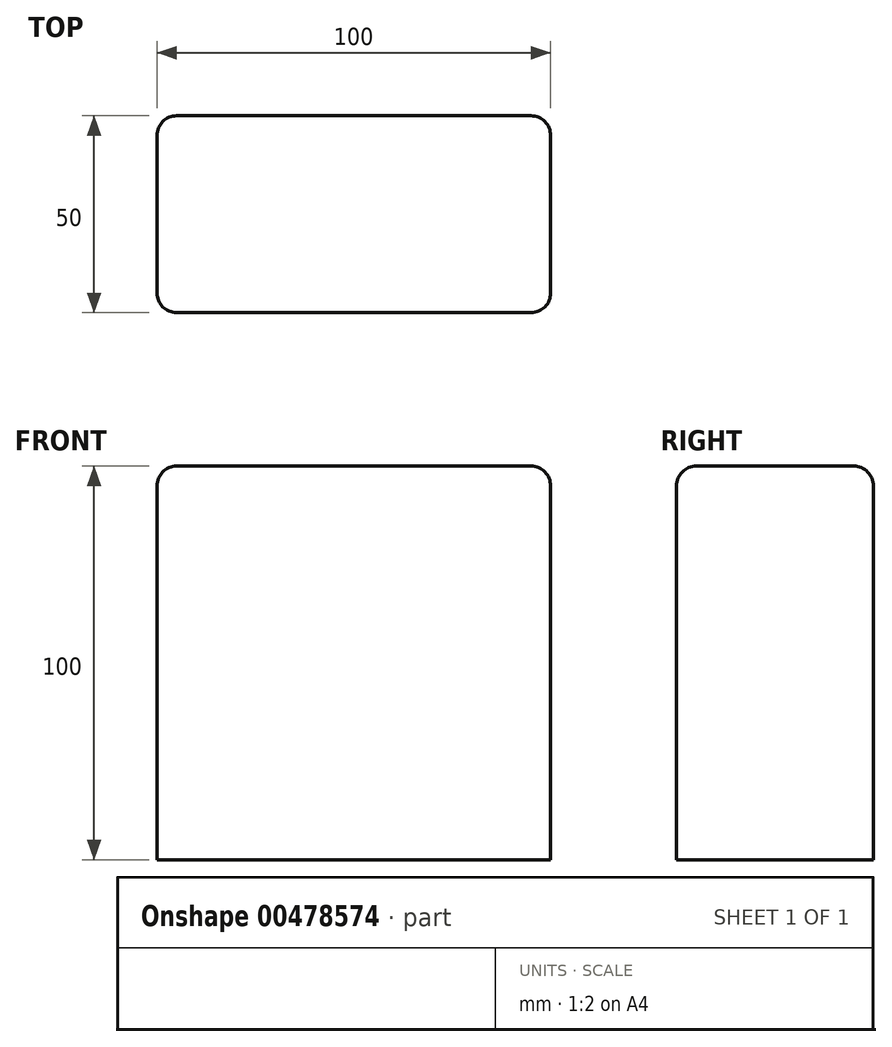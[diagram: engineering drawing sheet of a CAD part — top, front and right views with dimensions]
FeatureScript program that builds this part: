
annotation { "Feature Type Name" : "Feature", "Feature Type Description" : "" }
export const myFeature = defineFeature(function(context is Context, id is Id, definition is map)
    precondition{}
    {
        {
            var Q0;
            Q0=qCreatedBy(makeId("Top.planeOp"),FACE);
            var sketch = newSketch(context, id + "F0", { "sketchPlane" : qUnion([Q0])});
            skLineSegment(sketch, "E0.bottom", {"start": v(-40.12, 7.75) * mm, "end": v(59.88, 7.75) * mm});
            skLineSegment(sketch, "E0.top", {"start": v(-40.12, -42.25) * mm, "end": v(59.88, -42.25) * mm});
            skLineSegment(sketch, "E0.left", {"start": v(-40.12, 7.75) * mm, "end": v(-40.12, -42.25) * mm});
            skLineSegment(sketch, "E0.right", {"start": v(59.88, 7.75) * mm, "end": v(59.88, -42.25) * mm});
            skSolve(sketch);
        }
        {
            var Q0;
            Q0=makeQuery(id+"F0.imprint","IMPRINT",FACE,{"disambiguationData":[TD([[makeQuery(id+"F0.imprint","IMPRINT",EDGE,{"derivedFrom":sQuery(id+"F0.wireOp",EDGE,"E0.bottom")}),-1.0]])]});
            extrude(context, id + "F1", {"entities" : qUnion([Q0]), "depth" : 100 * mm});
        }
        {
            var Q0;
            Q0=makeQuery(id+"F1.opExtrude","CAP_EDGE",EDGE,{"disambiguationData":[OSD([sQuery(id+"F0.wireOp",EDGE,"E0.top")])],"isStart":false});
            var Q1;
            Q1=makeQuery(id+"F1.opExtrude","CAP_EDGE",EDGE,{"disambiguationData":[OSD([sQuery(id+"F0.wireOp",EDGE,"E0.bottom")])],"isStart":false});
            var Q2;
            Q2=makeQuery(id+"F1.opExtrude","CAP_FACE",FACE,{"disambiguationData":[OSD([sQuery(id+"F0.wireOp",EDGE,"E0.bottom"),sQuery(id+"F0.wireOp",EDGE,"E0.top"),sQuery(id+"F0.wireOp",EDGE,"E0.left"),sQuery(id+"F0.wireOp",EDGE,"E0.right")])],"isStart":false});
            var Q3;
            Q3=makeQuery(id+"F1.opExtrude","SWEPT_EDGE",EDGE,{"disambiguationData":[OSD([sQuery(id+"F0.wireOp",EDGE,"E0.bottom"),sQuery(id+"F0.wireOp",EDGE,"E0.right")])]});
            var Q4;
            Q4=makeQuery(id+"F1.opExtrude","SWEPT_EDGE",EDGE,{"disambiguationData":[OSD([sQuery(id+"F0.wireOp",EDGE,"E0.bottom"),sQuery(id+"F0.wireOp",EDGE,"E0.left")])]});
            var Q5;
            Q5=makeQuery(id+"F1.opExtrude","SWEPT_EDGE",EDGE,{"disambiguationData":[OSD([sQuery(id+"F0.wireOp",EDGE,"E0.top"),sQuery(id+"F0.wireOp",EDGE,"E0.left")])]});
            var Q6;
            Q6=makeQuery(id+"F1.opExtrude","SWEPT_EDGE",EDGE,{"disambiguationData":[OSD([sQuery(id+"F0.wireOp",EDGE,"E0.top"),sQuery(id+"F0.wireOp",EDGE,"E0.right")])]});
            fillet(context, id + "F2", {"entities" : qUnion([Q0, Q1, Q2, Q3, Q4, Q5, Q6]), "radius" : 5 * mm, "tangentPropagation" : true, "allowEdgeOverflow" : false});
        }
    });
